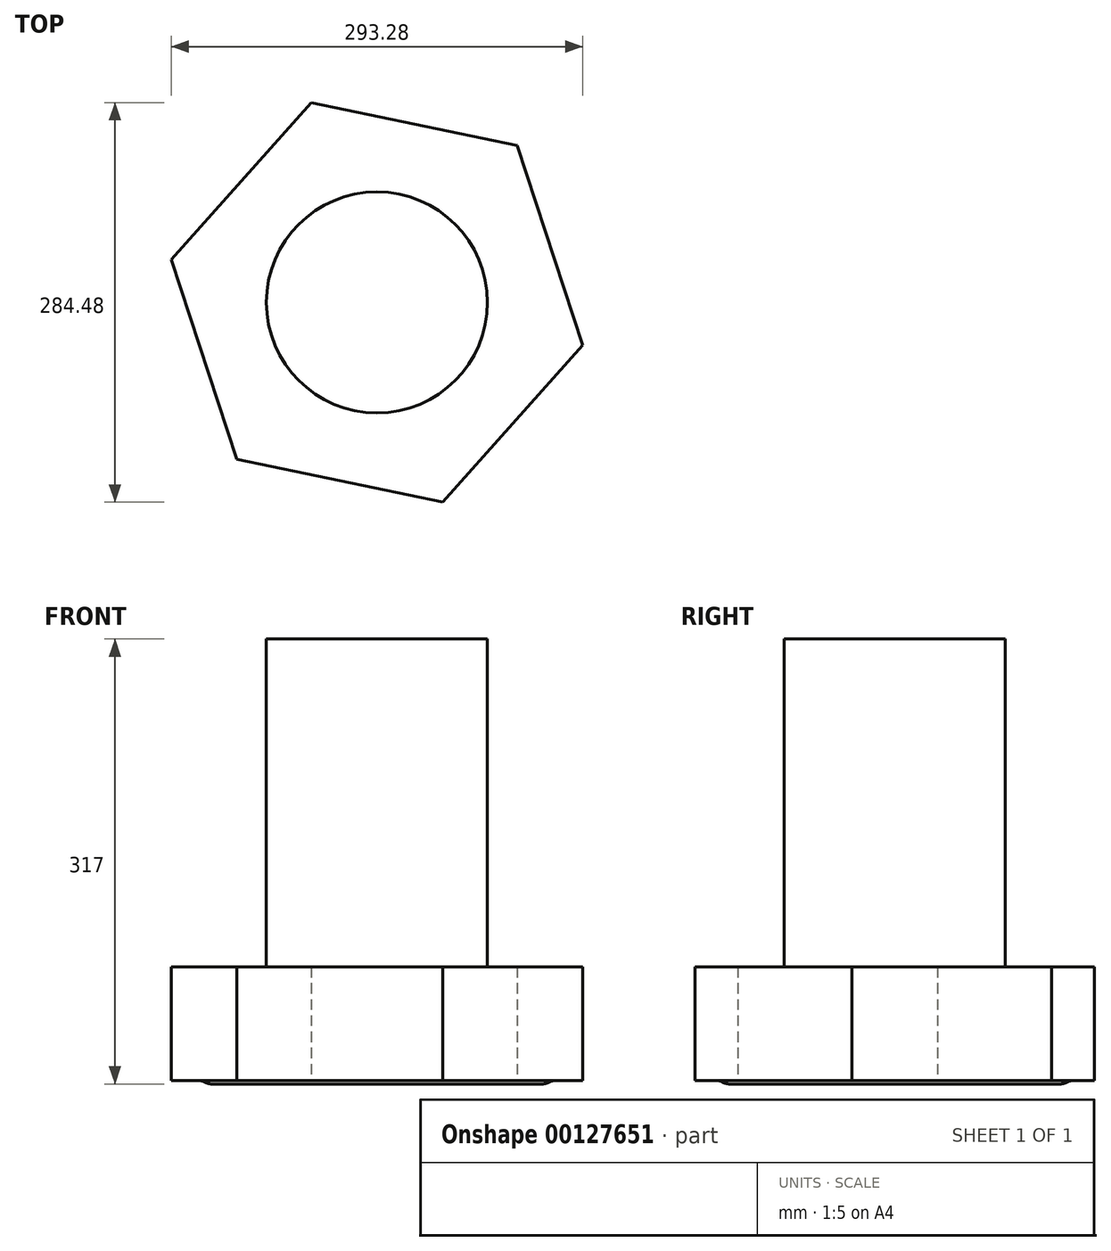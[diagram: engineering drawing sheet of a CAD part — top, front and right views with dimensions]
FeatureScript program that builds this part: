
annotation { "Feature Type Name" : "Feature", "Feature Type Description" : "" }
export const myFeature = defineFeature(function(context is Context, id is Id, definition is map)
    precondition{}
    {
        {
            var Q0;
            Q0=qCreatedBy(makeId("Top.planeOp"),FACE);
            var sketch = newSketch(context, id + "F0", { "sketchPlane" : qUnion([Q0])});
            skCircle(sketch, "E0.cCircle", {"center": v(0, 0) * mm, "radius": 129.7 * mm, "construction": true});
            skLineSegment(sketch, "E0.0", {"start": v(146.64, -30.49) * mm, "end": v(46.92, -142.24) * mm});
            skLineSegment(sketch, "E0.1", {"start": v(46.92, -142.24) * mm, "end": v(-99.72, -111.75) * mm});
            skLineSegment(sketch, "E0.2", {"start": v(-99.72, -111.75) * mm, "end": v(-146.64, 30.49) * mm});
            skLineSegment(sketch, "E0.3", {"start": v(-146.64, 30.49) * mm, "end": v(-46.92, 142.24) * mm});
            skLineSegment(sketch, "E0.4", {"start": v(-46.92, 142.24) * mm, "end": v(99.72, 111.75) * mm});
            skLineSegment(sketch, "E0.5", {"start": v(99.72, 111.75) * mm, "end": v(146.64, -30.49) * mm});
            skPoint(sketch, "E0.0.midPoint", {"position": v(96.78, -86.36) * mm});
            skSolve(sketch);
        }
        {
            var Q0;
            Q0 = qSketchRegion(id + "F0", true);
            extrude(context, id + "F1", {"entities" : qUnion([Q0]), "depth" : 81.03 * mm});
        }
        {
            var Q0;
            Q0=makeQuery(id+"F1.opExtrude","CAP_FACE",FACE,{"disambiguationData":[OSD([sQuery(id+"F0.wireOp",EDGE,"E0.0"),sQuery(id+"F0.wireOp",EDGE,"E0.1"),sQuery(id+"F0.wireOp",EDGE,"E0.2"),sQuery(id+"F0.wireOp",EDGE,"E0.3"),sQuery(id+"F0.wireOp",EDGE,"E0.4"),sQuery(id+"F0.wireOp",EDGE,"E0.5")])],"isStart":false});
            var sketch = newSketch(context, id + "F2", { "sketchPlane" : qUnion([Q0])});
            skCircle(sketch, "E1", {"center": v(0, 0) * mm, "radius": 78.74 * mm});
            skSolve(sketch);
        }
        {
            var Q0;
            Q0 = qSketchRegion(id + "F2", true);
            extrude(context, id + "F3", {"entities" : qUnion([Q0]), "operationType" : NewBodyOperationType.ADD, "depth" : 233.68 * mm});
        }
        {
            var Q0;
            Q0=makeQuery(id+"F1.opExtrude","CAP_FACE",FACE,{"disambiguationData":[OSD([sQuery(id+"F0.wireOp",EDGE,"E0.0"),sQuery(id+"F0.wireOp",EDGE,"E0.1"),sQuery(id+"F0.wireOp",EDGE,"E0.2"),sQuery(id+"F0.wireOp",EDGE,"E0.3"),sQuery(id+"F0.wireOp",EDGE,"E0.4"),sQuery(id+"F0.wireOp",EDGE,"E0.5")])],"isStart":true});
            var sketch = newSketch(context, id + "F4", { "sketchPlane" : qUnion([Q0])});
            skCircle(sketch, "E2", {"center": v(0, 0) * mm, "radius": 124.36 * mm});
            skSolve(sketch);
        }
        {
            var Q0;
            Q0 = qSketchRegion(id + "F4", true);
            extrude(context, id + "F5", {"entities" : qUnion([Q0]), "operationType" : NewBodyOperationType.ADD, "depth" : 2.3 * mm});
        }
        {
            var Q0;
            Q0=makeQuery(id+"F5.opExtrude","CAP_EDGE",EDGE,{"disambiguationData":[OSD([sQuery(id+"F4.wireOp",EDGE,"E2")])],"isStart":false});
            fillet(context, id + "F6", {"entities" : qUnion([Q0]), "radius" : 10.66 * mm, "tangentPropagation" : true, "allowEdgeOverflow" : false});
        }
        {
            var Q0;
            Q0=makeQuery(id+"F6.opFillet","BLEND_EDGE",EDGE,{"blendedFrom":[makeQuery(id+"F5.opExtrude","CAP_EDGE",EDGE,{"disambiguationData":[OSD([sQuery(id+"F4.wireOp",EDGE,"E2")])],"isStart":false}),makeQuery(id+"F1.opExtrude","CAP_FACE",FACE,{"disambiguationData":[OSD([sQuery(id+"F0.wireOp",EDGE,"E0.0"),sQuery(id+"F0.wireOp",EDGE,"E0.1"),sQuery(id+"F0.wireOp",EDGE,"E0.2"),sQuery(id+"F0.wireOp",EDGE,"E0.3"),sQuery(id+"F0.wireOp",EDGE,"E0.4"),sQuery(id+"F0.wireOp",EDGE,"E0.5")])],"isStart":true})],"blendedInto":[makeQuery(id+"F1.opExtrude","CAP_FACE",FACE,{"disambiguationData":[OSD([sQuery(id+"F0.wireOp",EDGE,"E0.0"),sQuery(id+"F0.wireOp",EDGE,"E0.1"),sQuery(id+"F0.wireOp",EDGE,"E0.2"),sQuery(id+"F0.wireOp",EDGE,"E0.3"),sQuery(id+"F0.wireOp",EDGE,"E0.4"),sQuery(id+"F0.wireOp",EDGE,"E0.5")])],"isStart":true})]});
            fillet(context, id + "F7", {"entities" : qUnion([Q0]), "radius" : 5.08 * mm, "tangentPropagation" : true, "allowEdgeOverflow" : false});
        }
    });
